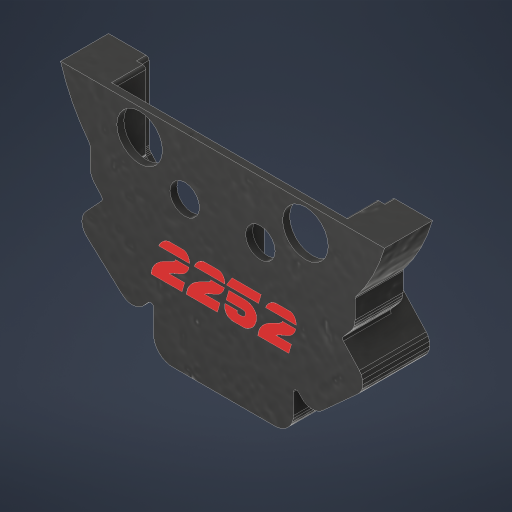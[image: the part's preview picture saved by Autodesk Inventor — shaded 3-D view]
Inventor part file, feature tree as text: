
AUTODESK INVENTOR PART (.ipt)
format: ipt  version: 2023 (Build 270158000, 158)  size: 3,560,960 bytes
history: native  units: in
note: dims shown in document units (in); Inventor stores cm internally (conversion verified against a paired STEP export)
features: other x10, extrude x9, sketch x8, projected_geometry x7, fillet x2, plane x1, reference x1
ambient origin geometry x8: Origin, YZ Plane, XZ Plane, XY Plane, X Axis, Y Axis, Z Axis, Center Point
bodies: Solid1 (feature_tree), Solid2 (feature_tree), Solid3 (feature_tree), Solid4 (feature_tree), Solid5 (feature_tree), Solid6 (feature_tree), Solid7 (feature_tree), Solid8 (feature_tree), Solid9 (feature_tree)
feature tree (38):
  other  "kraken-power-adapter.iam"
  other  "92916A325_Brass Washer.iam:1::SOLID.ipt:1"
  other  "93465A147_Brass Socket Head Screw.iam:1::SOLID_1.ipt:1"
  other  "92916A325_Brass Washer.iam:2::SOLID.ipt:1"
  other  "93465A147_Brass Socket Head Screw.iam:2::SOLID_1.ipt:1"
  other  "1335G1 IN HSG.iam:1::SOLID_2.ipt:1"
  other  "1335G1 IN HSG.iam:2::SOLID_2.ipt:1"
  other  "kraken-power-adapter PCB.ipt:1"
  plane  "Work Plane1"
  sketch  "Sketch2"  dims[d0=0.3937in d2=-0.3248in]
  extrude  "Extrusion1"  [1 undecoded]
  extrude  "Extrusion3"  Depth=0.0787in
  extrude  "Extrusion4"  Depth=0.1181in
  extrude  "Extrusion5"  Depth=0.1181in
  extrude  "Extrusion6"  Depth=1.0in TaperAngle=0.0deg
  fillet  "Fillet3"  Radius=1.0in
  extrude  "Extrusion7"  Depth=1.0in TaperAngle=0.0deg
  extrude  "Extrusion8"  Depth=0.0039in
  fillet  "Fillet4"  Radius=1.0in
  extrude  "Extrusion9"  Depth=0.3189in
  extrude  "Extrusion10"  Depth=2.2835in
  projected_geometry  "Projected Loop1"
  sketch  "Sketch4"  dims[d4=0.0787in d5=0.0787in]
  sketch  "Sketch5"  dims[d6=0.0787in d7=0.1181in]
  projected_geometry  "Projected Loop4"
  projected_geometry  "Projected Loop5"
  sketch  "Sketch6"  dims[d8=0.1181in d9=0.1181in]
  sketch  "Sketch7"  dims[d10=0.0472in d11=0.0in d15=1.0in d16=0.0in d18=1.0in]
  reference  "Reference1"
  projected_geometry  "Projected Loop6"
  sketch  "Sketch8"  dims[d19=0.0472in d20=1.0in d21=0.0in]
  projected_geometry  "Projected Loop7"
  projected_geometry  "Projected Loop8"
  sketch  "Sketch9"  dims[d23=0.0197in d24=0.0039in d25=1.0in d26=0.0in]
  sketch  "Sketch10"  dims[d27=0.0197in d28=0.3189in d29=2.2835in d30=1.0in d31=0.0in d32=0.0787in d33=0.0079in d34=0.4528in d35=0.0in d36=0.4528in d37=0.0in d38=0.0197in d39=0.0079in d40=0.0in d41=0.0079in d42=0.0in d12=0.5in d13=0.0344in d14=0.5in]
  projected_geometry  "Projected Loop9"
  other  "Assembly1"
  other  "kraken-can-adapter:1"
note: 1 required parameter value undecoded (feature->parameter linkage not recoverable at this tier; creation-order binding heuristic only, values carry confidence <= 0.55)
